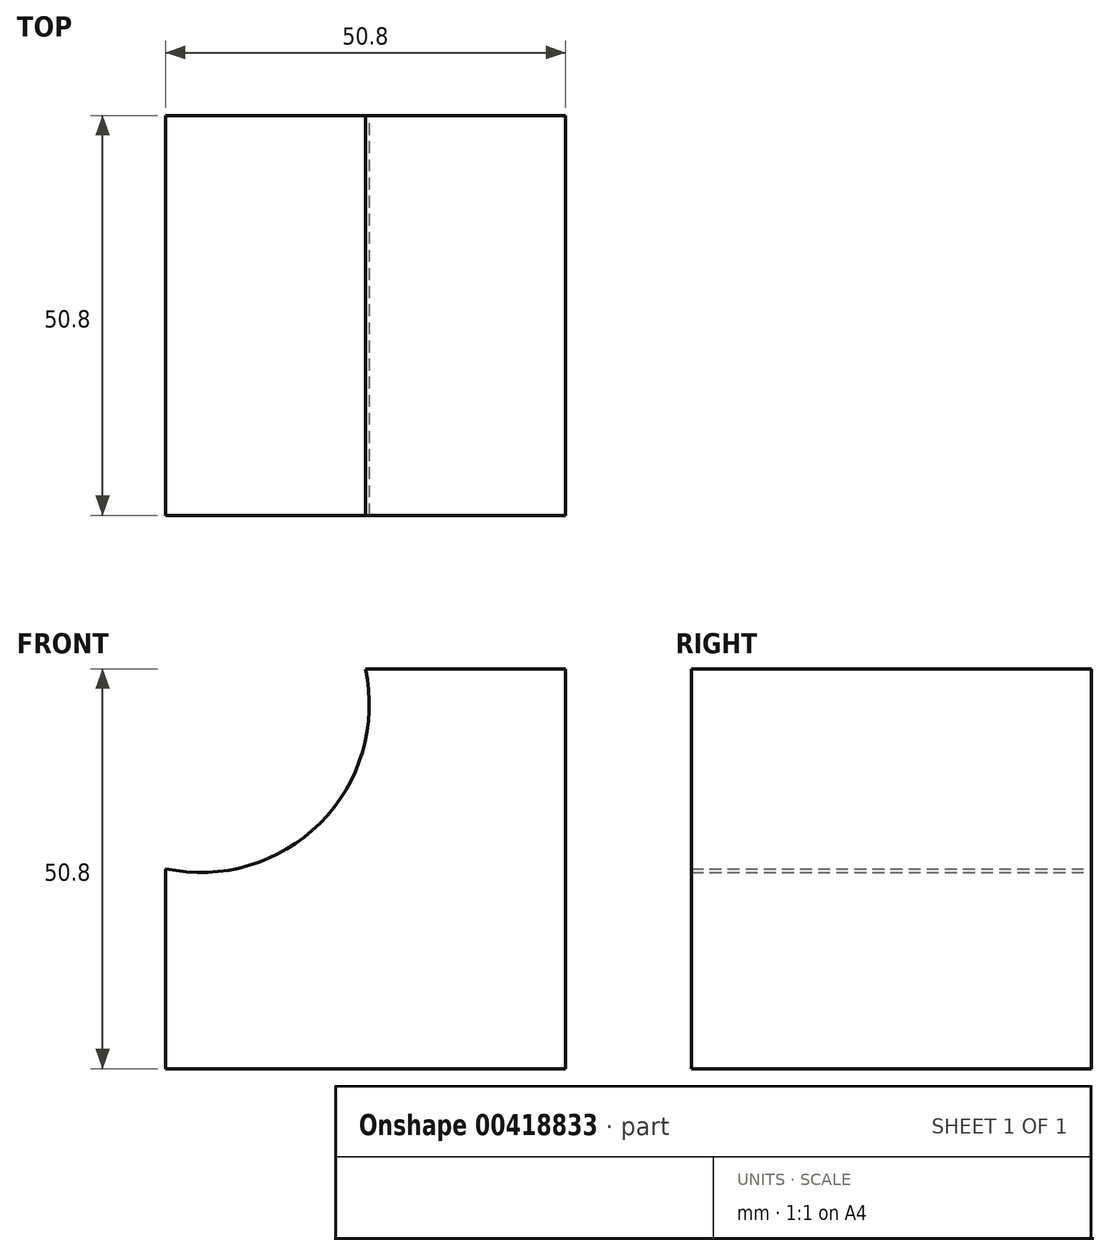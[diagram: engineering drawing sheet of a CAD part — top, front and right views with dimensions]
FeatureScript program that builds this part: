
annotation { "Feature Type Name" : "Feature", "Feature Type Description" : "" }
export const myFeature = defineFeature(function(context is Context, id is Id, definition is map)
    precondition{}
    {
        {
            var Q0;
            Q0=qCreatedBy(makeId("Front.planeOp"),FACE);
            var sketch = newSketch(context, id + "F0", { "sketchPlane" : qUnion([Q0])});
            skLineSegment(sketch, "E0", {"start": v(0, 0) * mm, "end": v(-50.8, 0) * mm});
            skLineSegment(sketch, "E1", {"start": v(0, 0) * mm, "end": v(0, 50.8) * mm});
            skLineSegment(sketch, "E2", {"start": v(0, 50.8) * mm, "end": v(-25.4, 50.8) * mm});
            skLineSegment(sketch, "E3", {"start": v(-50.8, 0) * mm, "end": v(-50.8, 25.4) * mm});
            skArc(sketch, "E4", {"start": v(-50.8, 25.4) * mm, "mid": v(-31.18, 31.18) * mm, "end": v(-25.4, 50.8) * mm});
            skSolve(sketch);
        }
        {
            var Q0;
            Q0 = qSketchRegion(id + "F0", true);
            extrude(context, id + "F1", {"entities" : qUnion([Q0]), "depth" : 50.8 * mm});
        }
    });
